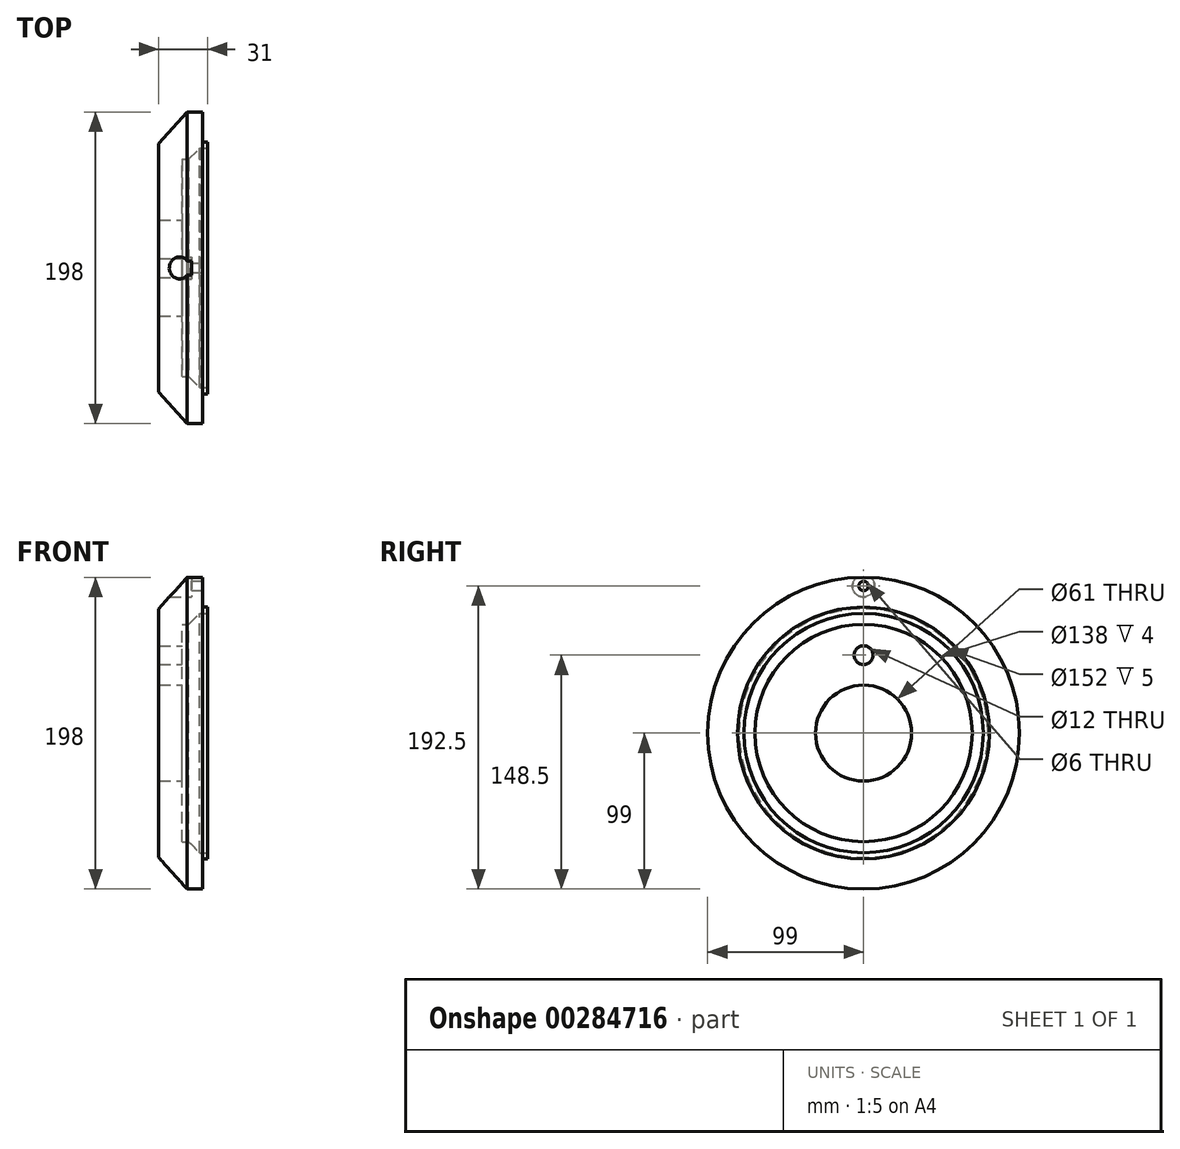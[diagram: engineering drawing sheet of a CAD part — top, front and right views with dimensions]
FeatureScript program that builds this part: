
annotation { "Feature Type Name" : "Feature", "Feature Type Description" : "" }
export const myFeature = defineFeature(function(context is Context, id is Id, definition is map)
    precondition{}
    {
        {
            var Q0;
            Q0=qCreatedBy(makeId("Front.planeOp"),FACE);
            var sketch = newSketch(context, id + "F0", { "sketchPlane" : qUnion([Q0])});
            skLineSegment(sketch, "E0", {"start": v(0, 0) * mm, "end": v(0, 80) * mm});
            skLineSegment(sketch, "E1", {"start": v(0, 80) * mm, "end": v(-5, 80) * mm});
            skLineSegment(sketch, "E2", {"start": v(-5, 80) * mm, "end": v(-5, 76) * mm});
            skLineSegment(sketch, "E3", {"start": v(-5, 76) * mm, "end": v(0, 76) * mm});
            skLineSegment(sketch, "E4", {"start": v(0, 0) * mm, "end": v(-31, 0) * mm, "construction": true});
            skLineSegment(sketch, "E5", {"start": v(-31, 0) * mm, "end": v(-31, 30.5) * mm});
            skLineSegment(sketch, "E6", {"start": v(-31, 30.5) * mm, "end": v(-16, 30.5) * mm});
            skLineSegment(sketch, "E7", {"start": v(0, 80) * mm, "end": v(-3, 80) * mm});
            skLineSegment(sketch, "E8", {"start": v(-3, 80) * mm, "end": v(-3, 99) * mm});
            skLineSegment(sketch, "E9", {"start": v(-31, 30.5) * mm, "end": v(-31, 79) * mm});
            skLineSegment(sketch, "E10", {"start": v(-3, 99) * mm, "end": v(-13, 99) * mm});
            skLineSegment(sketch, "E11", {"start": v(-13, 99) * mm, "end": v(-31, 79) * mm});
            skLineSegment(sketch, "E12", {"start": v(-16, 30.5) * mm, "end": v(-16, 69) * mm});
            skLineSegment(sketch, "E13", {"start": v(-16, 69) * mm, "end": v(-12, 69) * mm});
            skLineSegment(sketch, "E14", {"start": v(-12, 69) * mm, "end": v(-5, 76) * mm});
            skSolve(sketch);
        }
        {
            var Q0;
            Q0=qSketchRegion(id+"F0",true);
            var Q1;
            Q1=sQuery(id+"F0.wireOp",EDGE,"E4");
            revolve(context, id + "F1", {"entities" : qUnion([Q0]), "axis" : qUnion([Q1]), "revolveType" : RevolveType.FULL});
        }
        {
            var Q0;
            Q0=qCreatedBy(makeId("Right.planeOp"),FACE);
            cPlane(context, id + "F2", {"entities" : qUnion([Q0]), "cplaneType" : CPlaneType.OFFSET, "offset" : 16 * mm, "oppositeDirection" : true, "width" : 150 * mm, "height" : 150 * mm});
        }
        {
            var Q0;
            Q0=qCreatedBy(id+"F2.planeOp",FACE);
            var sketch = newSketch(context, id + "F3", { "sketchPlane" : qUnion([Q0])});
            skPoint(sketch, "E15", {"position": v(0, 49.5) * mm});
            skCircle(sketch, "E16", {"center": v(0, 49.5) * mm, "radius": 6 * mm});
            skSolve(sketch);
        }
        {
            var Q0;
            Q0=qSketchRegion(id+"F3",true);
            extrude(context, id + "F4", {"entities" : qUnion([Q0]), "operationType" : NewBodyOperationType.REMOVE, "oppositeDirection" : true, "depth" : 31 * mm});
        }
        {
            var Q0;
            Q0=qCreatedBy(makeId("Right.planeOp"),FACE);
            cPlane(context, id + "F5", {"entities" : qUnion([Q0]), "cplaneType" : CPlaneType.OFFSET, "offset" : 3 * mm, "oppositeDirection" : true, "width" : 150 * mm, "height" : 150 * mm});
        }
        {
            var Q0;
            Q0=qCreatedBy(id+"F5.planeOp",FACE);
            var sketch = newSketch(context, id + "F6", { "sketchPlane" : qUnion([Q0])});
            skPoint(sketch, "E17", {"position": v(0, 93.5) * mm});
            skCircle(sketch, "E18", {"center": v(0, 93.5) * mm, "radius": 3 * mm});
            skSolve(sketch);
        }
        {
            var Q0;
            Q0=makeQuery(id+"F6.imprint","IMPRINT",FACE,{"disambiguationData":[TD([[makeQuery(id+"F6.imprint","IMPRINT",EDGE,{"derivedFrom":sQuery(id+"F6.wireOp",EDGE,"E18")}),1.0]])]});
            extrude(context, id + "F7", {"entities" : qUnion([Q0]), "operationType" : NewBodyOperationType.REMOVE, "oppositeDirection" : true, "depth" : 31 * mm});
        }
        {
            var Q0;
            Q0=qCreatedBy(makeId("Right.planeOp"),FACE);
            cPlane(context, id + "F8", {"entities" : qUnion([Q0]), "cplaneType" : CPlaneType.OFFSET, "offset" : 10 * mm, "oppositeDirection" : true, "width" : 150 * mm, "height" : 150 * mm});
        }
        {
            var Q0;
            Q0=qCreatedBy(id+"F8.planeOp",FACE);
            var sketch = newSketch(context, id + "F9", { "sketchPlane" : qUnion([Q0])});
            skPoint(sketch, "E19", {"position": v(0, 93.5) * mm});
            skCircle(sketch, "E20", {"center": v(0, 93.5) * mm, "radius": 7 * mm});
            skSolve(sketch);
        }
        {
            var Q0;
            Q0=qSketchRegion(id+"F9",true);
            extrude(context, id + "F10", {"entities" : qUnion([Q0]), "operationType" : NewBodyOperationType.REMOVE, "oppositeDirection" : true, "depth" : 21 * mm});
        }
    });
